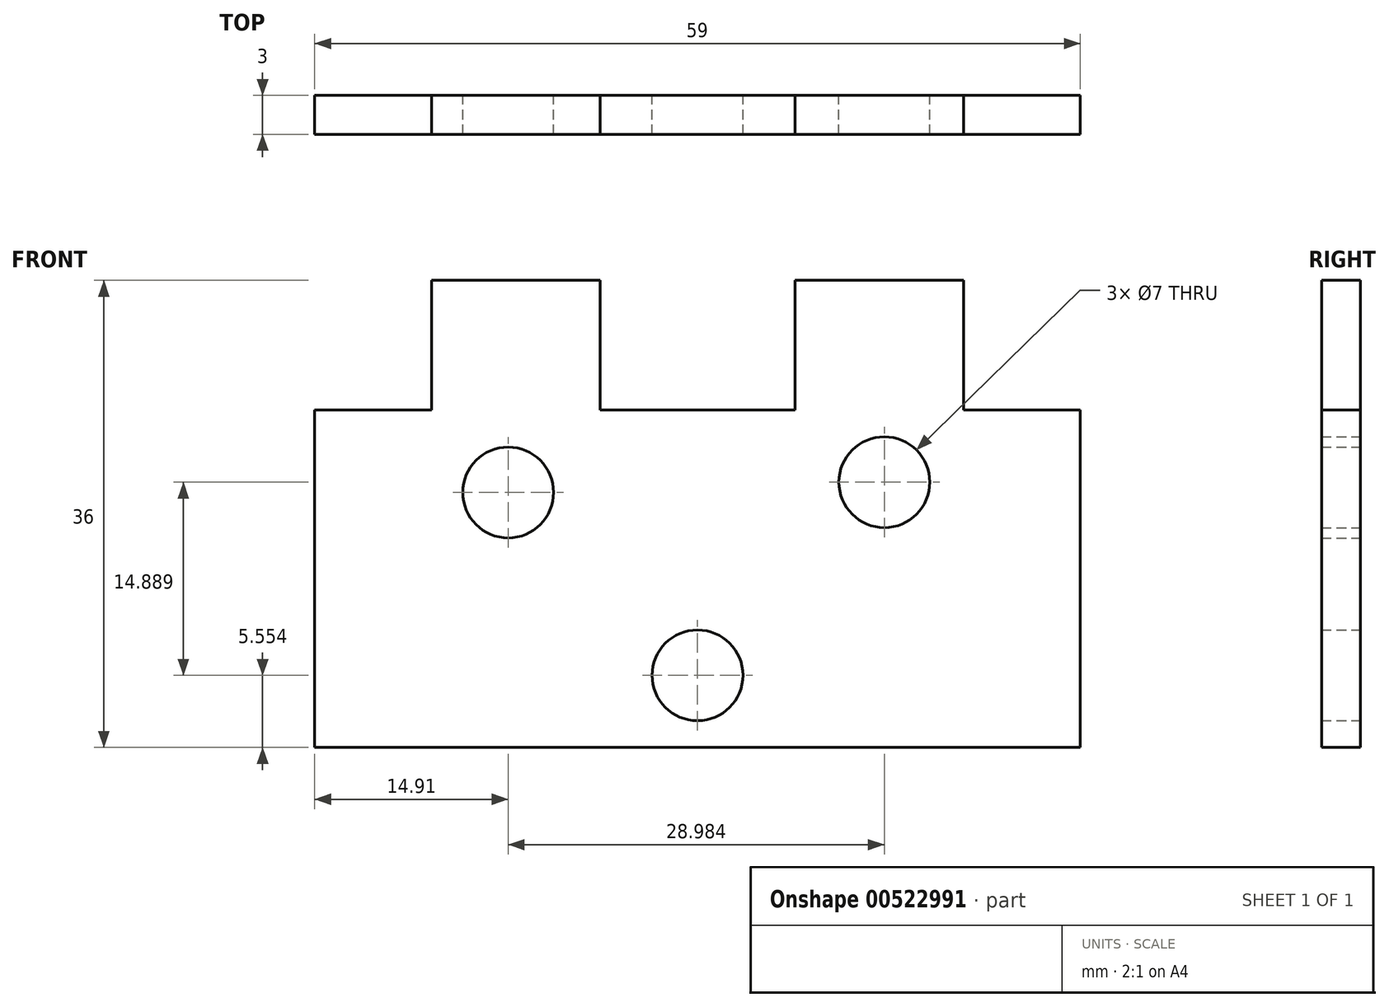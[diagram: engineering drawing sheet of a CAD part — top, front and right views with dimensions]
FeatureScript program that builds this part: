
annotation { "Feature Type Name" : "Feature", "Feature Type Description" : "" }
export const myFeature = defineFeature(function(context is Context, id is Id, definition is map)
    precondition{}
    {
        {
            var Q0;
            Q0=qCreatedBy(makeId("Front.planeOp"),FACE);
            var sketch = newSketch(context, id + "F0", { "sketchPlane" : qUnion([Q0])});
            skLineSegment(sketch, "E0.bottom", {"start": v(29.5, -13) * mm, "end": v(-29.5, -13) * mm});
            skLineSegment(sketch, "E0.top", {"start": v(29.5, 13) * mm, "end": v(-29.5, 13) * mm});
            skLineSegment(sketch, "E0.left", {"start": v(29.5, -13) * mm, "end": v(29.5, 13) * mm});
            skLineSegment(sketch, "E0.right", {"start": v(-29.5, -13) * mm, "end": v(-29.5, 13) * mm});
            skPoint(sketch, "E0.middle", {"position": v(0, 0) * mm});
            skLineSegment(sketch, "E1.bottom", {"start": v(-7.5, 13) * mm, "end": v(-20.5, 13) * mm});
            skLineSegment(sketch, "E1.top", {"start": v(-7.5, 23) * mm, "end": v(-20.5, 23) * mm});
            skLineSegment(sketch, "E1.left", {"start": v(-7.5, 13) * mm, "end": v(-7.5, 23) * mm});
            skLineSegment(sketch, "E1.right", {"start": v(-20.5, 13) * mm, "end": v(-20.5, 23) * mm});
            skPoint(sketch, "E1.middle", {"position": v(-14, 18) * mm});
            skLineSegment(sketch, "E2.bottom", {"start": v(20.5, 13) * mm, "end": v(7.5, 13) * mm});
            skLineSegment(sketch, "E2.top", {"start": v(20.5, 23) * mm, "end": v(7.5, 23) * mm});
            skLineSegment(sketch, "E2.left", {"start": v(20.5, 13) * mm, "end": v(20.5, 23) * mm});
            skLineSegment(sketch, "E2.right", {"start": v(7.5, 13) * mm, "end": v(7.5, 23) * mm});
            skPoint(sketch, "E2.middle", {"position": v(14, 18) * mm});
            skCircle(sketch, "E3", {"center": v(-14.6, 6.65) * mm, "radius": 3.5 * mm});
            skCircle(sketch, "E4", {"center": v(14.4, 7.44) * mm, "radius": 3.5 * mm});
            skCircle(sketch, "E5", {"center": v(0, -7.45) * mm, "radius": 3.5 * mm});
            skSolve(sketch);
        }
        {
            var Q0;
            Q0 = qSketchRegion(id + "F0", true);
            extrude(context, id + "F1", {"entities" : qUnion([Q0]), "endBound" : BoundingType.SYMMETRIC, "depth" : 3 * mm, "offsetDistance" : 25 * mm});
        }
    });
